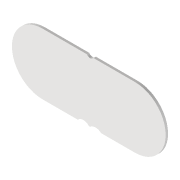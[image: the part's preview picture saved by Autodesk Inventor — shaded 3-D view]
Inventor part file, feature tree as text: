
AUTODESK INVENTOR PART (.ipt)
format: ipt  version: 2021 (Build 250183000, 183)  size: 91,136 bytes
history: native  units: mm
features: sketch x1, plane x1, extrude x1
ambient origin geometry x8: Origin, YZ Plane, XZ Plane, XY Plane, X Axis, Y Axis, Z Axis, Center Point
bodies: Volumenkörper1 (feature_tree)
feature tree (3):
  sketch  "Skizze1"  dims[d1=45.0mm d2=45.0mm d3=68.0mm d4=0.0mm d5=10.0mm d6=0.0mm]
  plane  "Arbeitsebene1"
  extrude  "Extrusion1"  Depth=45.0mm
